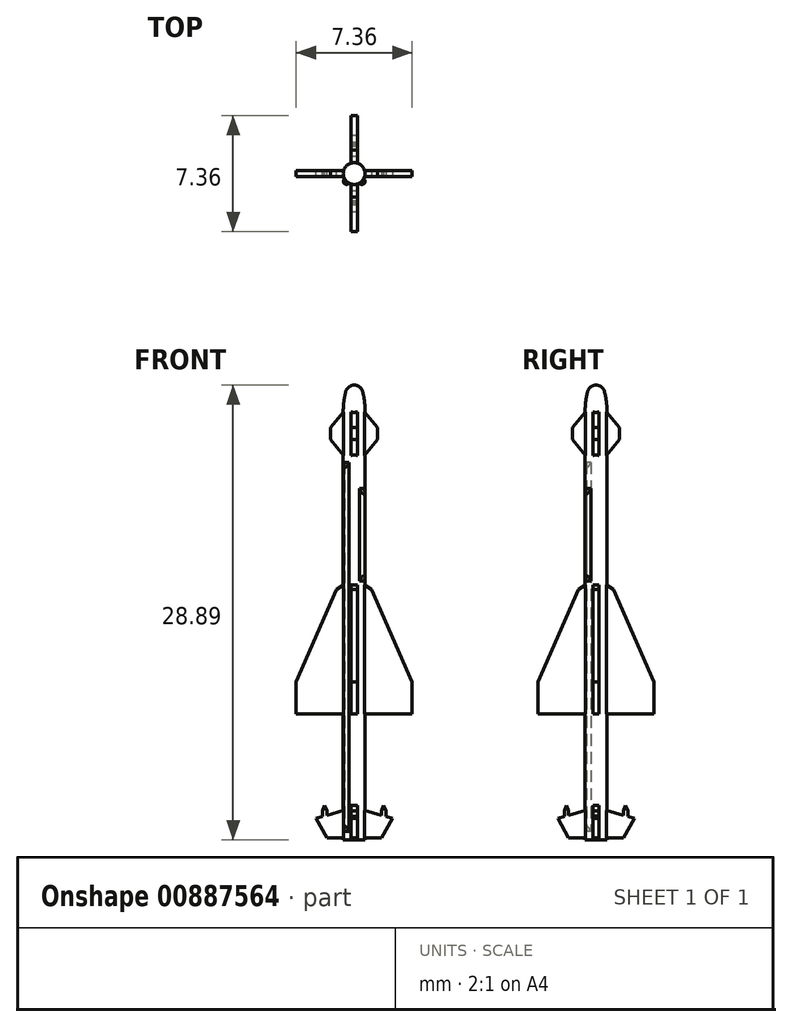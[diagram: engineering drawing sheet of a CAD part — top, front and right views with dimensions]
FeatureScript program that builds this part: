
annotation { "Feature Type Name" : "Feature", "Feature Type Description" : "" }
export const myFeature = defineFeature(function(context is Context, id is Id, definition is map)
    precondition{}
    {
        {
            var Q0;
            Q0=qCreatedBy(makeId("Front.planeOp"),FACE);
            var sketch = newSketch(context, id + "F0", { "sketchPlane" : qUnion([Q0])});
            skLineSegment(sketch, "E0", {"start": v(0, 0) * mm, "end": v(0, 28.89) * mm});
            skLineSegment(sketch, "E1", {"start": v(0.7, 27.22) * mm, "end": v(0.7, 0) * mm});
            skLineSegment(sketch, "E2", {"start": v(0.7, 0) * mm, "end": v(0, 0) * mm});
            skArc(sketch, "E3", {"start": v(0.54, 28.47) * mm, "mid": v(0.34, 28.77) * mm, "end": v(0, 28.89) * mm});
            skArc(sketch, "E4", {"start": v(0.7, 27.22) * mm, "mid": v(0.65, 27.85) * mm, "end": v(0.54, 28.47) * mm});
            skLineSegment(sketch, "E5", {"start": v(0, 28.89) * mm, "end": v(6.27, 28.89) * mm, "construction": true});
            skSolve(sketch);
        }
        {
            var Q0;
            Q0=makeQuery(id+"F0.imprint","IMPRINT",FACE,{"disambiguationData":[TD([[makeQuery(id+"F0.imprint","IMPRINT",EDGE,{"derivedFrom":sQuery(id+"F0.wireOp",EDGE,"E0")}),-1.0]])]});
            var Q1;
            Q1=sQuery(id+"F0.wireOp",EDGE,"E0");
            revolve(context, id + "F1", {"surfaceOperationType" : NewSurfaceOperationType.NEW, "entities" : qUnion([Q0]), "axis" : qUnion([Q1]), "revolveType" : RevolveType.FULL});
        }
        {
            var Q0;
            Q0=qCreatedBy(makeId("Front.planeOp"),FACE);
            var sketch = newSketch(context, id + "F2", { "sketchPlane" : qUnion([Q0])});
            skLineSegment(sketch, "E6.0", {"start": v(0.7, 27.22) * mm, "end": v(-0.7, 27.22) * mm, "construction": true});
            skLineSegment(sketch, "E7", {"start": v(0, 0.14) * mm, "end": v(1.74, 0.14) * mm});
            skLineSegment(sketch, "E8", {"start": v(2.43, 1.35) * mm, "end": v(0.7, 1.87) * mm});
            skLineSegment(sketch, "E9", {"start": v(0.4, 1.96) * mm, "end": v(0.4, 7.99) * mm});
            skLineSegment(sketch, "E10", {"start": v(0.4, 7.99) * mm, "end": v(3.68, 7.99) * mm});
            skLineSegment(sketch, "E11", {"start": v(0, 28) * mm, "end": v(0, 0.14) * mm});
            skLineSegment(sketch, "E12", {"start": v(0.7, 27.22) * mm, "end": v(0.7, 0) * mm, "construction": true});
            skLineSegment(sketch, "E13", {"start": v(0.7, 1.88) * mm, "end": v(0.4, 1.96) * mm});
            skLineSegment(sketch, "E14", {"start": v(1.74, 0.14) * mm, "end": v(2.43, 1.35) * mm});
            skLineSegment(sketch, "E15", {"start": v(3.68, 7.99) * mm, "end": v(3.68, 10.03) * mm});
            skLineSegment(sketch, "E16", {"start": v(0.4, 16.38) * mm, "end": v(0.4, 24.09) * mm});
            skLineSegment(sketch, "E17", {"start": v(1.5, 25.42) * mm, "end": v(0.4, 24.09) * mm});
            skLineSegment(sketch, "E18", {"start": v(1.5, 25.42) * mm, "end": v(1.5, 26.18) * mm});
            skLineSegment(sketch, "E19", {"start": v(1.5, 26.18) * mm, "end": v(0, 28) * mm});
            skLineSegment(sketch, "E20", {"start": v(1.74, 1.56) * mm, "end": v(1.74, 1.85) * mm});
            skLineSegment(sketch, "E21", {"start": v(1.74, 1.85) * mm, "end": v(1.87, 2.19) * mm});
            skLineSegment(sketch, "E22", {"start": v(1.87, 2.19) * mm, "end": v(2.01, 1.85) * mm});
            skLineSegment(sketch, "E23", {"start": v(2.01, 1.85) * mm, "end": v(2.01, 1.48) * mm});
            skLineSegment(sketch, "E24", {"start": v(3.68, 10.03) * mm, "end": v(1.11, 15.9) * mm});
            skLineSegment(sketch, "E25", {"start": v(1.11, 15.9) * mm, "end": v(0.4, 16.38) * mm});
            skPoint(sketch, "E26", {"position": v(0.7, 16.18) * mm});
            skPoint(sketch, "E27", {"position": v(0.7, 24.44) * mm});
            skPoint(sketch, "E28", {"position": v(0.7, 27.15) * mm});
            skSolve(sketch);
        }
        {
            var Q0;
            Q0=qSketchRegion(id+"F2",true);
            extrude(context, id + "F3", {"entities" : qUnion([Q0]), "operationType" : NewBodyOperationType.ADD, "oppositeDirection" : true, "depth" : .4 * mm, "offsetDistance" : 25 * mm, "symmetric" : true});
        }
        {
            var Q0;
            Q0=makeQuery(id+"F1.opRevolve","SWEPT_BODY",BODY,{"disambiguationData":[OSD([sQuery(id+"F0.wireOp",EDGE,"E0"),sQuery(id+"F0.wireOp",EDGE,"E1"),sQuery(id+"F0.wireOp",EDGE,"E2"),sQuery(id+"F0.wireOp",EDGE,"h1jDSi8t-veb7-85qg-XgDk-6E8DmZjBuz4r")])]});
            var Q1;
            Q1=makeQuery(id+"F1.opRevolve","SWEPT_FACE",FACE,{"disambiguationData":[OSD([sQuery(id+"F0.wireOp",EDGE,"E1")])]});
            circularPattern(context, id + "F4", {"operationType" : NewBodyOperationType.ADD, "entities" : qUnion([Q0]), "axis" : qUnion([Q1]), "angle" : 360 * degree, "instanceCount" : 4, "equalSpace" : true, "computeTransformsWithoutBuiltin" : true});
        }
        {
            var Q0;
            Q0=qCreatedBy(makeId("Top.planeOp"),FACE);
            cPlane(context, id + "F5", {"entities" : qUnion([Q0]), "cplaneType" : CPlaneType.OFFSET, "offset" : (140 / 144) * mm, "width" : 150 * mm, "height" : 150 * mm});
        }
        {
            var Q0;
            Q0=qCreatedBy(id+"F5.planeOp",FACE);
            var sketch = newSketch(context, id + "F6", { "sketchPlane" : qUnion([Q0])});
            skLineSegment(sketch, "E29", {"start": v(-0.63, -0.35) * mm, "end": v(-0.44, -0.15) * mm});
            skLineSegment(sketch, "E30", {"start": v(-0.44, -0.15) * mm, "end": v(-0.15, -0.44) * mm});
            skLineSegment(sketch, "E31", {"start": v(-0.15, -0.44) * mm, "end": v(-0.35, -0.63) * mm});
            skArc(sketch, "E32", {"start": v(-0.63, -0.35) * mm, "mid": v(-0.63, -0.63) * mm, "end": v(-0.35, -0.63) * mm});
            skLineSegment(sketch, "E33", {"start": v(-0.3, -0.3) * mm, "end": v(0, 0) * mm, "construction": true});
            skLineSegment(sketch, "E34", {"start": v(0, 0) * mm, "end": v(-0.48, 0) * mm, "construction": true});
            skSolve(sketch);
        }
        {
            var Q0;
            Q0=makeQuery(id+"F6.imprint","IMPRINT",FACE,{"disambiguationData":[TD([[makeQuery(id+"F6.imprint","IMPRINT",EDGE,{"derivedFrom":sQuery(id+"F6.wireOp",EDGE,"E29")}),-1.0]])]});
            extrude(context, id + "F7", {"entities" : qUnion([Q0]), "operationType" : NewBodyOperationType.ADD, "depth" : (3250 / 144) * mm, "offsetDistance" : 25 * mm});
        }
        {
            var Q0;
            Q0=qCreatedBy(makeId("Top.planeOp"),FACE);
            cPlane(context, id + "F8", {"entities" : qUnion([Q0]), "cplaneType" : CPlaneType.OFFSET, "offset" : (2430 / 144) * mm, "width" : 150 * mm, "height" : 150 * mm});
        }
        {
            var Q0;
            Q0=qCreatedBy(id+"F8.planeOp",FACE);
            var sketch = newSketch(context, id + "F9", { "sketchPlane" : qUnion([Q0])});
            skLineSegment(sketch, "E35", {"start": v(-0.05, -0.24) * mm, "end": v(0.24, 0.05) * mm});
            skLineSegment(sketch, "E36", {"start": v(0.24, 0.05) * mm, "end": v(0.64, -0.35) * mm});
            skLineSegment(sketch, "E37", {"start": v(0.35, -0.64) * mm, "end": v(-0.05, -0.24) * mm});
            skArc(sketch, "E38", {"start": v(0.35, -0.64) * mm, "mid": v(0.64, -0.64) * mm, "end": v(0.64, -0.35) * mm});
            skLineSegment(sketch, "E39", {"start": v(0, -0.58) * mm, "end": v(0, 0) * mm, "construction": true});
            skLineSegment(sketch, "E40", {"start": v(0, 0) * mm, "end": v(0.1, -0.1) * mm, "construction": true});
            skSolve(sketch);
        }
        {
            var Q0;
            Q0 = qSketchRegion(id + "F9", true);
            extrude(context, id + "F10", {"entities" : qUnion([Q0]), "operationType" : NewBodyOperationType.ADD, "depth" : (720 / 144) * mm, "offsetDistance" : 25 * mm});
        }
        {
            var Q0;
            Q0=makeQuery(id+"F7.boolean.opBoolean","INTERSECT",EDGE,{"derivedFrom":[makeQuery(id+"F1.opRevolve","SWEPT_FACE",FACE,{"disambiguationData":[OSD([sQuery(id+"F0.wireOp",EDGE,"E1")])]}),makeQuery(id+"F7.opExtrude","CAP_FACE",FACE,{"disambiguationData":[OSD([sQuery(id+"F6.wireOp",EDGE,"E29"),sQuery(id+"F6.wireOp",EDGE,"E30"),sQuery(id+"F6.wireOp",EDGE,"E31"),sQuery(id+"F6.wireOp",EDGE,"E32")])],"isStart":false})]});
            var Q1;
            Q1=makeQuery(id+"F7.boolean.opBoolean","INTERSECT",EDGE,{"derivedFrom":[makeQuery(id+"F1.opRevolve","SWEPT_FACE",FACE,{"disambiguationData":[OSD([sQuery(id+"F0.wireOp",EDGE,"E1")])]}),makeQuery(id+"F7.opExtrude","CAP_FACE",FACE,{"disambiguationData":[OSD([sQuery(id+"F6.wireOp",EDGE,"E29"),sQuery(id+"F6.wireOp",EDGE,"E30"),sQuery(id+"F6.wireOp",EDGE,"E31"),sQuery(id+"F6.wireOp",EDGE,"E32")])],"isStart":true})]});
            var Q2;
            Q2=makeQuery(id+"F10.boolean.opBoolean","INTERSECT",EDGE,{"derivedFrom":[makeQuery(id+"F1.opRevolve","SWEPT_FACE",FACE,{"disambiguationData":[OSD([sQuery(id+"F0.wireOp",EDGE,"E1")])]}),makeQuery(id+"F10.opExtrude","CAP_FACE",FACE,{"disambiguationData":[OSD([sQuery(id+"F9.wireOp",EDGE,"E35"),sQuery(id+"F9.wireOp",EDGE,"E36"),sQuery(id+"F9.wireOp",EDGE,"E37"),sQuery(id+"F9.wireOp",EDGE,"E38")])],"isStart":true})]});
            var Q3;
            Q3=makeQuery(id+"F10.boolean.opBoolean","INTERSECT",EDGE,{"derivedFrom":[makeQuery(id+"F1.opRevolve","SWEPT_FACE",FACE,{"disambiguationData":[OSD([sQuery(id+"F0.wireOp",EDGE,"E1")])]}),makeQuery(id+"F10.opExtrude","CAP_FACE",FACE,{"disambiguationData":[OSD([sQuery(id+"F9.wireOp",EDGE,"E35"),sQuery(id+"F9.wireOp",EDGE,"E36"),sQuery(id+"F9.wireOp",EDGE,"E37"),sQuery(id+"F9.wireOp",EDGE,"E38")])],"isStart":false})]});
            chamfer(context, id + "F11", {"entities" : qUnion([Q0, Q1, Q2, Q3]), "chamferType" : ChamferType.OFFSET_ANGLE, "width" : .25 * mm, "oppositeDirection" : true, "angle" : 60 * degree, "tangentPropagation" : true});
        }
    });
